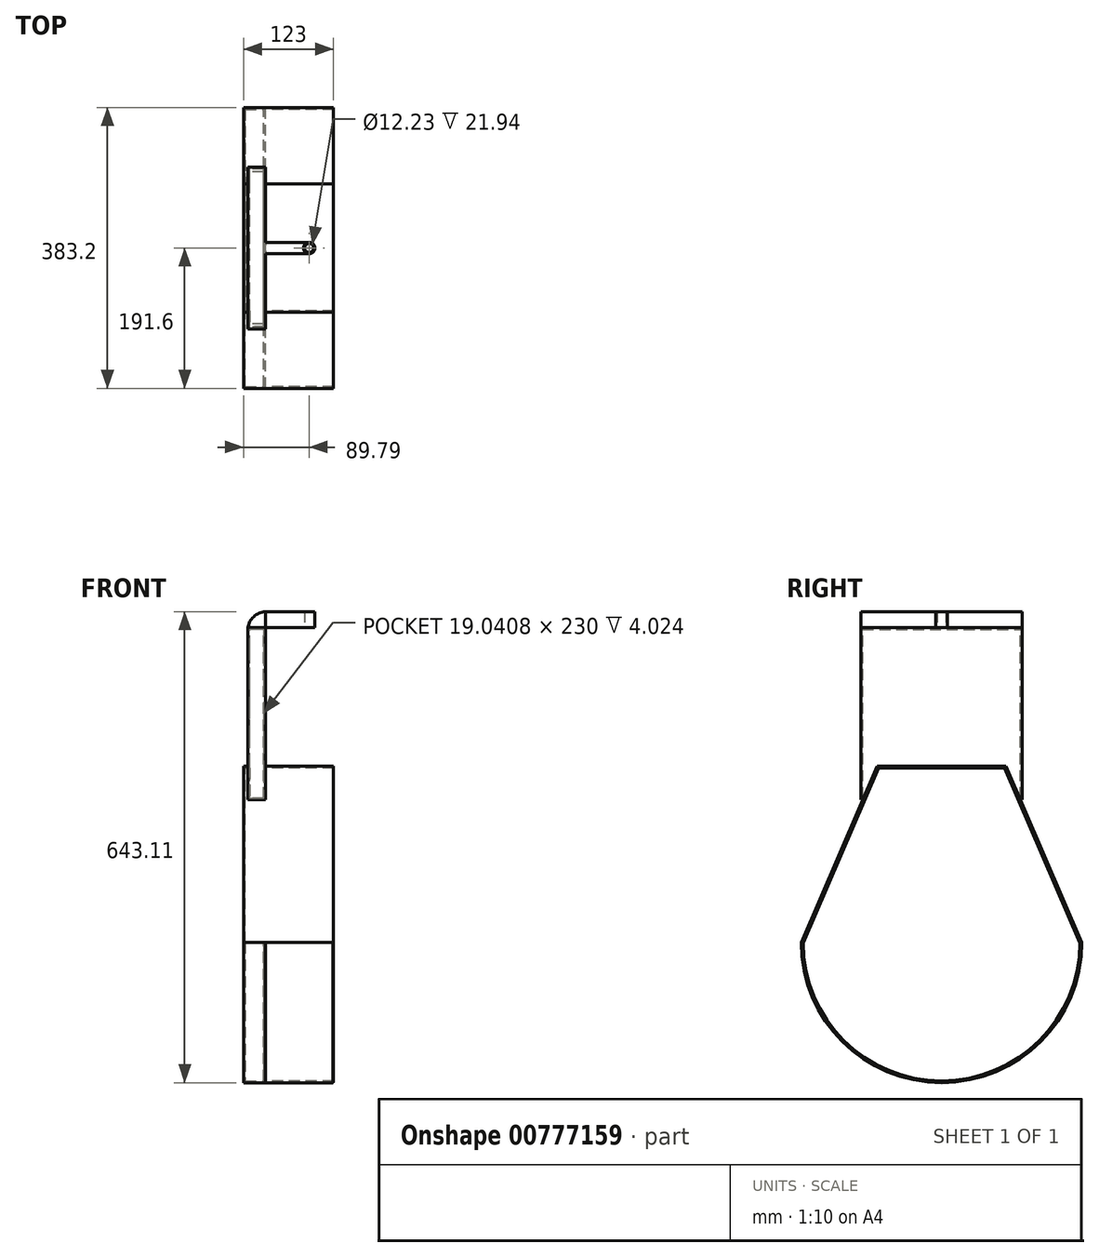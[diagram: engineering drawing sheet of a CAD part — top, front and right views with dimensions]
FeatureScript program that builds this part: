
annotation { "Feature Type Name" : "Feature", "Feature Type Description" : "" }
export const myFeature = defineFeature(function(context is Context, id is Id, definition is map)
    precondition{}
    {
        {
            var Q0;
            Q0=qCreatedBy(makeId("Top.planeOp"),FACE);
            var sketch = newSketch(context, id + "F0", { "sketchPlane" : qUnion([Q0])});
            skCircle(sketch, "E0", {"center": v(0, 0) * mm, "radius": 6.12 * mm});
            skCircle(sketch, "E1", {"center": v(0, 0) * mm, "radius": 7.76 * mm});
            skSolve(sketch);
        }
        {
            var Q0;
            Q0=makeQuery(id+"F0.imprint","IMPRINT",FACE,{"disambiguationData":[TD([[makeQuery(id+"F0.imprint","IMPRINT",EDGE,{"derivedFrom":sQuery(id+"F0.wireOp",EDGE,"E0")}),-1.0]])]});
            extrude(context, id + "F1", {"entities" : qUnion([Q0]), "depth" : 21.94 * mm, "offsetDistance" : 25 * mm});
        }
        {
            var Q0;
            Q0=makeQuery(id+"F1.opExtrude","CAP_FACE",FACE,{"disambiguationData":[OSD([sQuery(id+"F0.wireOp",EDGE,"E0"),sQuery(id+"F0.wireOp",EDGE,"E1")])],"isStart":true});
            var sketch = newSketch(context, id + "F2", { "sketchPlane" : qUnion([Q0])});
            skLineSegment(sketch, "E2", {"start": v(0, 7.76) * mm, "end": v(-59.8, 7.76) * mm});
            skLineSegment(sketch, "E3.MirrorCS", {"start": v(0, -7.76) * mm, "end": v(-59.8, -7.76) * mm});
            skLineSegment(sketch, "E4", {"start": v(-59.8, 7.76) * mm, "end": v(-59.8, 110.32) * mm});
            skLineSegment(sketch, "E5", {"start": v(-59.8, 110.32) * mm, "end": v(-83.83, 110.32) * mm});
            skLineSegment(sketch, "E6", {"start": v(-83.83, 110.32) * mm, "end": v(-83.83, 0) * mm});
            skLineSegment(sketch, "E7.MirrorCS", {"start": v(-59.8, -7.76) * mm, "end": v(-59.8, -110.32) * mm});
            skLineSegment(sketch, "E8.MirrorCS", {"start": v(-59.8, -110.32) * mm, "end": v(-83.83, -110.32) * mm});
            skLineSegment(sketch, "E9.MirrorCS", {"start": v(-83.83, -110.32) * mm, "end": v(-83.83, 0) * mm});
            skSolve(sketch);
        }
        {
            var Q0;
            {var subQ1=sQuery(id+"F2.wireOp",EDGE,"E2");Q0=makeQuery(id+"F2.imprint","IMPRINT",FACE,{"disambiguationData":[TD([[makeQuery(id+"F2.imprint","IMPRINT",EDGE,{"derivedFrom":subQ1}),1.0]])]});}
            extrude(context, id + "F3", {"entities" : qUnion([Q0]), "operationType" : NewBodyOperationType.ADD, "oppositeDirection" : true, "depth" : 21.9 * mm, "offsetDistance" : 25 * mm});
        }
        {
            var Q0;
            Q0=makeQuery(id+"F3.opExtrude","CAP_EDGE",EDGE,{"disambiguationData":[OSD([sQuery(id+"F2.wireOp",EDGE,"E6"),sQuery(id+"F2.wireOp",EDGE,"E9.MirrorCS")])],"isStart":false});
            fillet(context, id + "F4", {"entities" : qUnion([Q0]), "radius" : 26.07 * mm, "tangentPropagation" : true, "allowEdgeOverflow" : false});
        }
        {
            var Q0;
            {var subQ0=sQuery(id+"F0.wireOp",EDGE,"E1");Q0=makeQuery(id+"F3.boolean.opBoolean","MERGE",FACE,{"derivedFrom":[makeQuery(id+"F1.opExtrude","CAP_FACE",FACE,{"disambiguationData":[OSD([sQuery(id+"F0.wireOp",EDGE,"E0"),subQ0])],"isStart":true}),makeQuery(id+"F3.opExtrude","CAP_FACE",FACE,{"disambiguationData":[OSD([subQ0,sQuery(id+"F2.wireOp",EDGE,"E2"),sQuery(id+"F2.wireOp",EDGE,"E3.MirrorCS"),sQuery(id+"F2.wireOp",EDGE,"E4"),sQuery(id+"F2.wireOp",EDGE,"E5"),sQuery(id+"F2.wireOp",EDGE,"E7.MirrorCS"),sQuery(id+"F2.wireOp",EDGE,"E8.MirrorCS"),sQuery(id+"F2.wireOp",EDGE,"E6"),sQuery(id+"F2.wireOp",EDGE,"E9.MirrorCS")])],"isStart":true})]});}
            var sketch = newSketch(context, id + "F5", { "sketchPlane" : qUnion([Q0])});
            skLineSegment(sketch, "E10", {"start": v(-83.83, -110.32) * mm, "end": v(-59.8, -110.32) * mm});
            skLineSegment(sketch, "E11", {"start": v(-59.8, -110.32) * mm, "end": v(-59.8, 110.32) * mm});
            skLineSegment(sketch, "E12", {"start": v(-59.8, 110.32) * mm, "end": v(-83.83, 110.32) * mm});
            skLineSegment(sketch, "E13", {"start": v(-83.83, 110.32) * mm, "end": v(-83.83, -110.32) * mm});
            skSolve(sketch);
        }
        {
            var Q0;
            Q0=makeQuery(id+"FdrR8GfU2UdsVuI_1.boolean.opBoolean","MERGE",FACE,{"derivedFrom":[makeQuery(id+"F3.opExtrude","SWEPT_FACE",FACE,{"disambiguationData":[OSD([sQuery(id+"F2.wireOp",EDGE,"E7.MirrorCS")])]}),makeQuery(id+"FdrR8GfU2UdsVuI_1.opExtrude","SWEPT_FACE",FACE,{"disambiguationData":[OSD([sQuery(id+"F5.wireOp",EDGE,"E11")])]})]});
            var sketch = newSketch(context, id + "F6", { "sketchPlane" : qUnion([Q0])});
            skArc(sketch, "E14", {"start": v(-191.6, -429.56) * mm, "mid": v(0, -621.17) * mm, "end": v(191.6, -429.56) * mm});
            skLineSegment(sketch, "E15", {"start": v(87.77, -189.07) * mm, "end": v(-87.77, -189.07) * mm});
            skLineSegment(sketch, "E16", {"start": v(191.6, -429.56) * mm, "end": v(87.77, -189.07) * mm});
            skLineSegment(sketch, "E17", {"start": v(-191.6, -429.56) * mm, "end": v(-87.77, -189.07) * mm});
            skSolve(sketch);
        }
        {
            var Q0;
            Q0=makeQuery(id+"F6.imprint","IMPRINT",FACE,{"disambiguationData":[TD([[makeQuery(id+"F6.imprint","IMPRINT",EDGE,{"derivedFrom":sQuery(id+"F6.wireOp",EDGE,"E14")}),1.0]])]});
            extrude(context, id + "F7", {"entities" : qUnion([Q0]), "operationType" : NewBodyOperationType.ADD, "oppositeDirection" : true, "depth" : 30 * mm, "offsetDistance" : 25 * mm});
        }
        {
            var Q0;
            {var subQ3=sQuery(id+"F5.wireOp",EDGE,"E10");Q0=makeQuery(id+"F5.imprint","IMPRINT",FACE,{"disambiguationData":[TD([[makeQuery(id+"F5.imprint","IMPRINT",EDGE,{"derivedFrom":subQ3}),-1.0]])]});}
            extrude(context, id + "F8", {"entities" : qUnion([Q0]), "depth" : 235 * mm, "offsetDistance" : 25 * mm});
        }
        {
            var Q0;
            Q0=makeQuery(id+"F7.opExtrude","CAP_FACE",FACE,{"disambiguationData":[OSD([sQuery(id+"F6.wireOp",EDGE,"E14"),sQuery(id+"F6.wireOp",EDGE,"E15"),sQuery(id+"F6.wireOp",EDGE,"E16"),sQuery(id+"F6.wireOp",EDGE,"E17")])],"isStart":true});
            var sketch = newSketch(context, id + "F9", { "sketchPlane" : qUnion([Q0])});
            skArc(sketch, "E18", {"start": v(-191.6, -429.56) * mm, "mid": v(0, -621.1) * mm, "end": v(191.6, -429.56) * mm});
            skSolve(sketch);
        }
        {
            var Q0;
            Q0=makeQuery(id+"F9.imprint","IMPRINT",FACE,{"disambiguationData":[TD([[makeQuery(id+"F9.imprint","IMPRINT",EDGE,{"derivedFrom":sQuery(id+"F9.wireOp",EDGE,"E18")}),1.0]])]});
            extrude(context, id + "F10", {"entities" : qUnion([Q0]), "operationType" : NewBodyOperationType.ADD, "depth" : 93 * mm, "offsetDistance" : 25 * mm});
        }
        {
            var Q0;
            Q0=makeQuery(id+"F10.opExtrude","CAP_FACE",FACE,{"disambiguationData":[OSD([sQuery(id+"F9.wireOp",EDGE,"E18"),sQuery(id+"F9.wireOp",EDGE,"mT1IJWeS-oks0-Yn4V-Zlnh-kEzUsgIpfcTl")])],"isStart":false});
            shell(context, id + "F11", {"entities" : qUnion([Q0]), "thickness" : 2.5 * mm});
        }
        {
            var Q0;
            {var subQ0=sQuery(id+"F6.wireOp",EDGE,"E16");var subQ1=sQuery(id+"F6.wireOp",EDGE,"E15");var subQ2=sQuery(id+"F6.wireOp",EDGE,"E17");var subQ3=sQuery(id+"F6.wireOp",EDGE,"E14");var subQ4=makeQuery(id+"F7.opExtrude","CAP_FACE",FACE,{"disambiguationData":[OSD([subQ3,subQ1,subQ0,subQ2])],"isStart":true});Q0=makeQuery(id+"F10.boolean.opBoolean","SPLIT",FACE,{"disambiguationData":[TD([makeQuery(id+"F7.opExtrude","SWEPT_FACE",FACE,{"disambiguationData":[OSD([subQ3])]}),subQ4,makeQuery(id+"F7.opExtrude","SWEPT_FACE",FACE,{"disambiguationData":[OSD([subQ1])]}),makeQuery(id+"F7.opExtrude","SWEPT_FACE",FACE,{"disambiguationData":[OSD([subQ0])]}),makeQuery(id+"F7.opExtrude","SWEPT_FACE",FACE,{"disambiguationData":[OSD([subQ2])]}),makeQuery(id+"F10.opExtrude","SWEPT_FACE",FACE,{"disambiguationData":[OSD([sQuery(id+"F9.wireOp",EDGE,"E18")])]}),makeQuery(id+"F10.opExtrude","SWEPT_FACE",FACE,{"disambiguationData":[OSD([sQuery(id+"F9.wireOp",EDGE,"mT1IJWeS-oks0-Yn4V-Zlnh-kEzUsgIpfcTl")])]})])],"derivedFrom":subQ4});}
            extrude(context, id + "F12", {"entities" : qUnion([Q0]), "depth" : 92 * mm, "offsetDistance" : 25 * mm});
        }
    });
